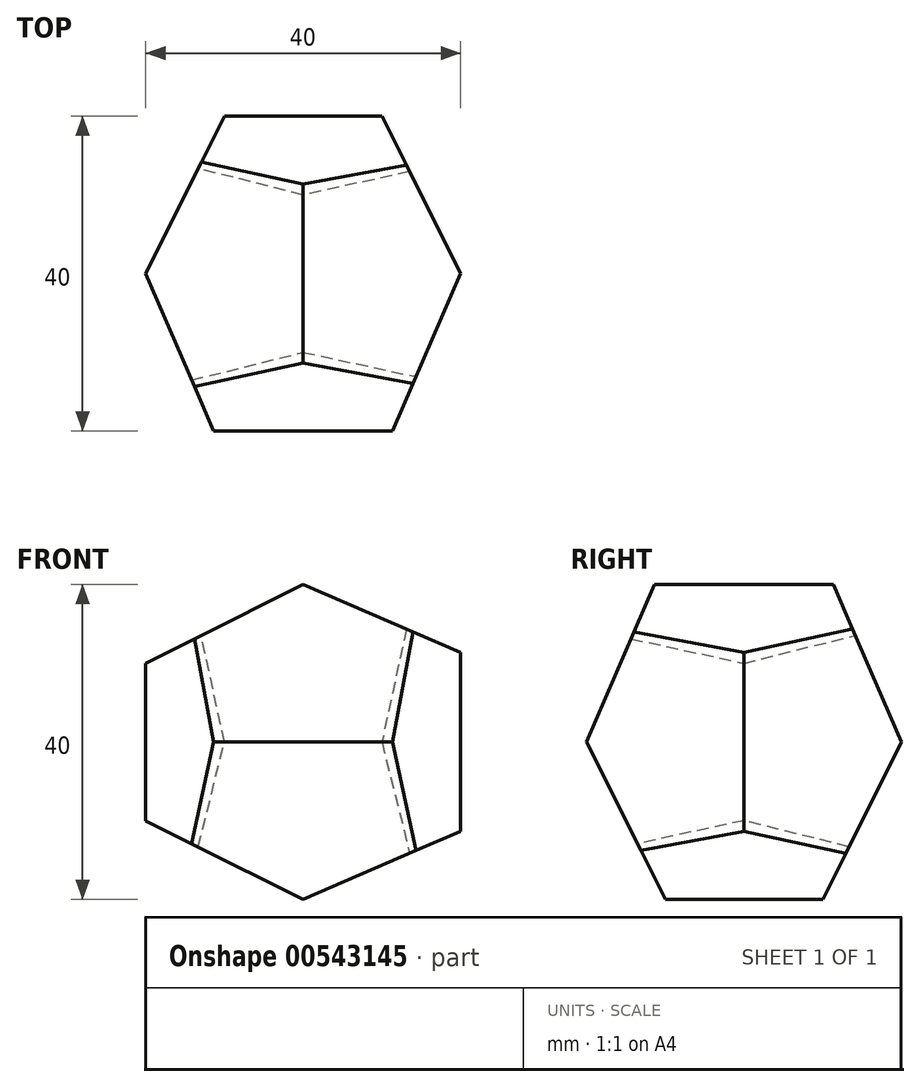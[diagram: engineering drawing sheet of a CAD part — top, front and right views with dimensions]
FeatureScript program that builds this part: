
annotation { "Feature Type Name" : "Feature", "Feature Type Description" : "" }
export const myFeature = defineFeature(function(context is Context, id is Id, definition is map)
    precondition{}
    {
        {
            var Q0;
            Q0=qCreatedBy(makeId("Front.planeOp"),FACE);
            var sketch = newSketch(context, id + "F0", { "sketchPlane" : qUnion([Q0])});
            skLineSegment(sketch, "E0", {"start": v(46.28, 0) * mm, "end": v(0, 20) * mm});
            skLineSegment(sketch, "E1", {"start": v(0, 20) * mm, "end": v(-40, 0) * mm});
            skLineSegment(sketch, "E2", {"start": v(-40, 0) * mm, "end": v(0, -20) * mm});
            skLineSegment(sketch, "E3", {"start": v(0, -20) * mm, "end": v(46.28, 0) * mm});
            skSolve(sketch);
        }
        {
            var Q0;
            Q0=makeQuery(id+"F0.imprint","IMPRINT",FACE,{"disambiguationData":[TD([[makeQuery(id+"F0.imprint","IMPRINT",EDGE,{"derivedFrom":sQuery(id+"F0.wireOp",EDGE,"E0")}),1.0]])]});
            extrude(context, id + "F1", {"entities" : qUnion([Q0]), "depth" : 25 * mm, "offsetDistance" : 25 * mm, "hasSecondDirection" : true, "secondDirectionOppositeDirection" : true, "secondDirectionDepth" : 25 * mm});
        }
        {
            var Q0;
            Q0=qCreatedBy(makeId("Front.planeOp"),FACE);
            var sketch = newSketch(context, id + "F2", { "sketchPlane" : qUnion([Q0])});
            skLineSegment(sketch, "E4", {"start": v(0, 49.78) * mm, "end": v(0, 0) * mm});
            skSolve(sketch);
        }
        {
            var Q0;
            Q0=qCreatedBy(makeId("Front.planeOp"),FACE);
            var sketch = newSketch(context, id + "F3", { "sketchPlane" : qUnion([Q0])});
            skLineSegment(sketch, "E5", {"start": v(60.84, 0) * mm, "end": v(0, 0) * mm});
            skSolve(sketch);
        }
        {
            var Q0;
            Q0=qCreatedBy(makeId("Right.planeOp"),FACE);
            var sketch = newSketch(context, id + "F4", { "sketchPlane" : qUnion([Q0])});
            skLineSegment(sketch, "E6", {"start": v(48.72, 0) * mm, "end": v(-1.84, 0) * mm});
            skSolve(sketch);
        }
        {
            var Q0;
            Q0=makeQuery(id+"F1.opExtrude","SWEPT_BODY",BODY,{"disambiguationData":[OSD([sQuery(id+"F0.wireOp",EDGE,"E0"),sQuery(id+"F0.wireOp",EDGE,"E1"),sQuery(id+"F0.wireOp",EDGE,"E2"),sQuery(id+"F0.wireOp",EDGE,"E3")])]});
            var Q1;
            Q1=sQuery(id+"F2.wireOp",EDGE,"E4");
            transform(context, id + "F5", {"entities" : qUnion([Q0]), "transformType" : TransformType.ROTATION, "transformAxis" : qUnion([Q1]), "angle" : 90 * degree, "makeCopy" : true});
        }
        {
            var Q0;
            Q0=makeQuery(id+"F5.opPattern","COPY",BODY,{"derivedFrom":makeQuery(id+"F1.opExtrude","SWEPT_BODY",BODY,{"disambiguationData":[OSD([sQuery(id+"F0.wireOp",EDGE,"E0"),sQuery(id+"F0.wireOp",EDGE,"E1"),sQuery(id+"F0.wireOp",EDGE,"E2"),sQuery(id+"F0.wireOp",EDGE,"E3")])]}),"instanceName":"1"});
            var Q1;
            Q1=sQuery(id+"F4.wireOp",EDGE,"E6");
            transform(context, id + "F6", {"entities" : qUnion([Q0]), "transformType" : TransformType.ROTATION, "transformAxis" : qUnion([Q1]), "angle" : 90 * degree, "makeCopy" : true});
        }
        {
            var Q0;
            Q0=makeQuery(id+"F5.opPattern","COPY",BODY,{"derivedFrom":makeQuery(id+"F1.opExtrude","SWEPT_BODY",BODY,{"disambiguationData":[OSD([sQuery(id+"F0.wireOp",EDGE,"E0"),sQuery(id+"F0.wireOp",EDGE,"E1"),sQuery(id+"F0.wireOp",EDGE,"E2"),sQuery(id+"F0.wireOp",EDGE,"E3")])]}),"instanceName":"1"});
            var Q1;
            Q1=sQuery(id+"F3.wireOp",EDGE,"E5");
            transform(context, id + "F7", {"entities" : qUnion([Q0]), "transformType" : TransformType.ROTATION, "transformAxis" : qUnion([Q1]), "angle" : 90 * degree, "makeCopy" : false});
        }
        {
            var Q0;
            Q0=makeQuery(id+"F5.opPattern","COPY",BODY,{"derivedFrom":makeQuery(id+"F1.opExtrude","SWEPT_BODY",BODY,{"disambiguationData":[OSD([sQuery(id+"F0.wireOp",EDGE,"E0"),sQuery(id+"F0.wireOp",EDGE,"E1"),sQuery(id+"F0.wireOp",EDGE,"E2"),sQuery(id+"F0.wireOp",EDGE,"E3")])]}),"instanceName":"1"});
            var Q1;
            Q1=makeQuery(id+"F6.opPattern","COPY",BODY,{"derivedFrom":makeQuery(id+"F5.opPattern","COPY",BODY,{"derivedFrom":makeQuery(id+"F1.opExtrude","SWEPT_BODY",BODY,{"disambiguationData":[OSD([sQuery(id+"F0.wireOp",EDGE,"E0"),sQuery(id+"F0.wireOp",EDGE,"E1"),sQuery(id+"F0.wireOp",EDGE,"E2"),sQuery(id+"F0.wireOp",EDGE,"E3")])]}),"instanceName":"1"}),"instanceName":"1"});
            booleanBodies(context, id + "F8", {"operationType" : BooleanOperationType.INTERSECTION, "tools" : qUnion([Q0, Q1])});
        }
        {
            var Q0;
            {var subQ0=makeQuery(id+"F5.opPattern","COPY",BODY,{"derivedFrom":makeQuery(id+"F1.opExtrude","SWEPT_BODY",BODY,{"disambiguationData":[OSD([sQuery(id+"F0.wireOp",EDGE,"E0"),sQuery(id+"F0.wireOp",EDGE,"E1"),sQuery(id+"F0.wireOp",EDGE,"E2"),sQuery(id+"F0.wireOp",EDGE,"E3")])]}),"instanceName":"1"});Q0=makeQuery(id+"F8.opBoolean","INTERSECT",BODY,{"derivedFrom":[subQ0,makeQuery(id+"F6.opPattern","COPY",BODY,{"derivedFrom":subQ0,"instanceName":"1"})]});}
            var Q1;
            Q1=makeQuery(id+"F1.opExtrude","SWEPT_BODY",BODY,{"disambiguationData":[OSD([sQuery(id+"F0.wireOp",EDGE,"E0"),sQuery(id+"F0.wireOp",EDGE,"E1"),sQuery(id+"F0.wireOp",EDGE,"E2"),sQuery(id+"F0.wireOp",EDGE,"E3")])]});
            booleanBodies(context, id + "F9", {"operationType" : BooleanOperationType.INTERSECTION, "tools" : qUnion([Q0, Q1])});
        }
    });
